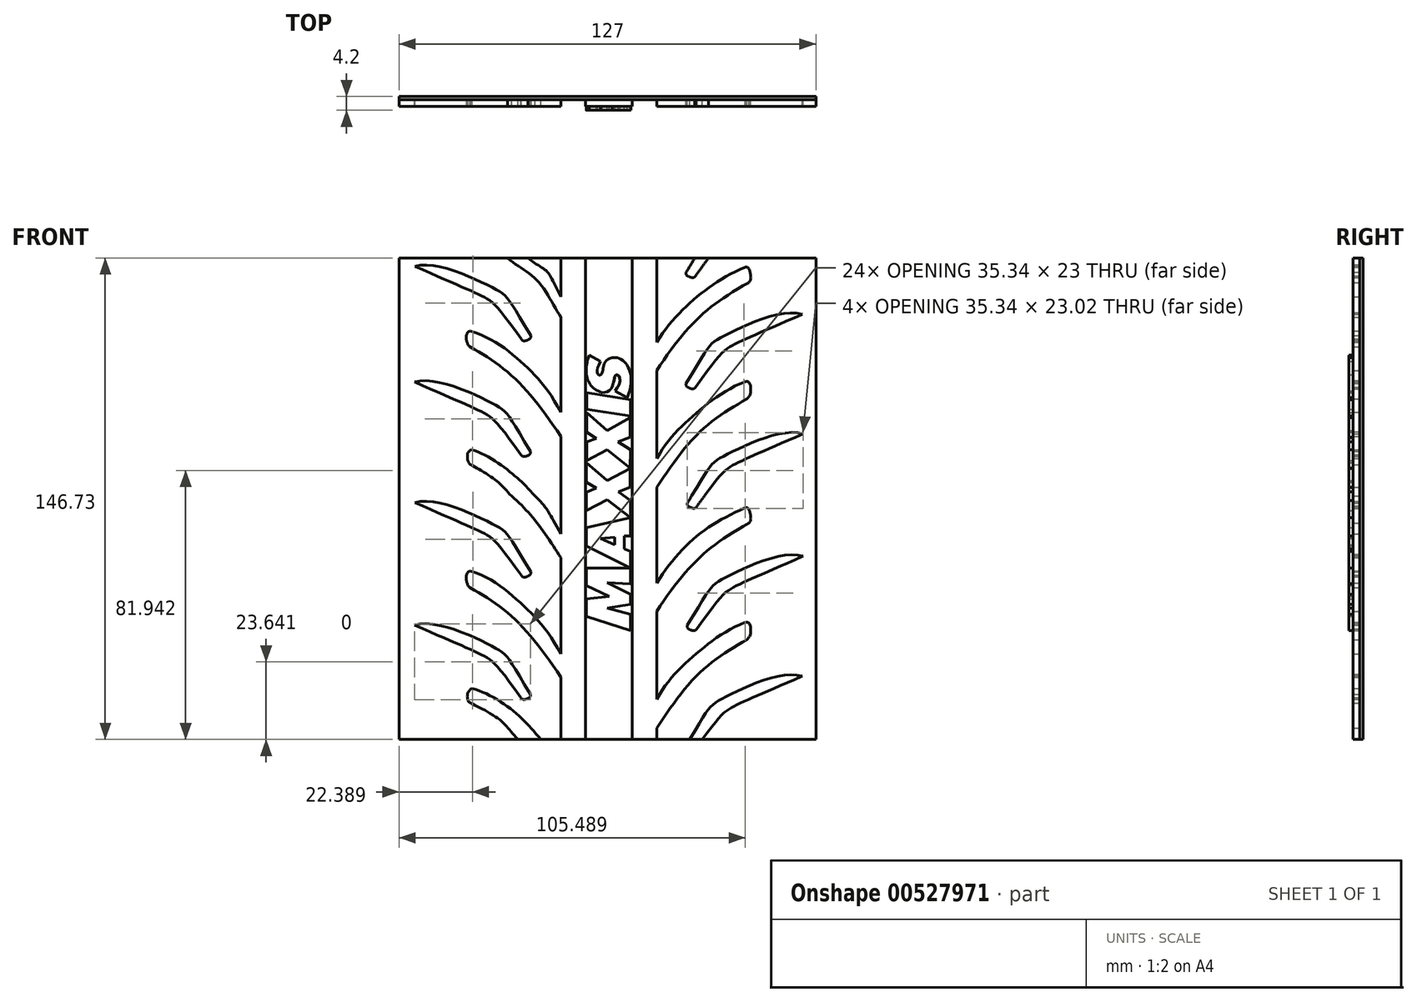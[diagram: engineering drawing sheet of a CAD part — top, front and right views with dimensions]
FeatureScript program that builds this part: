
annotation { "Feature Type Name" : "Feature", "Feature Type Description" : "" }
export const myFeature = defineFeature(function(context is Context, id is Id, definition is map)
    precondition{}
    {
        {
            var Q0;
            Q0=qCreatedBy(makeId("Front.planeOp"),FACE);
            var sketch = newSketch(context, id + "F0", { "sketchPlane" : qUnion([Q0])});
            skFitSpline(sketch, "E0", {"points": [v(-41.87, 15.25) * mm, v(-26, 5.1) * mm, v(-14.16, -10.06) * mm], "startDerivative": vector(39.83, -11.03) * mm, "endDerivative": vector(22.53, -43.37) * mm});
            skFitSpline(sketch, "E1", {"points": [v(-41.87, 15.25) * mm, v(-41.87, 10.2) * mm], "startDerivative": vector(-5.4, -1.6) * mm, "endDerivative": vector(3.38, -2.64) * mm});
            skFitSpline(sketch, "E2", {"points": [v(-41.87, 10.2) * mm, v(-28.68, 1) * mm, v(-14.16, -17.08) * mm], "startDerivative": vector(31.36, -16.8) * mm, "endDerivative": vector(27.1, -40.96) * mm});
            skLineSegment(sketch, "E3", {"start": v(-14.16, 38.05) * mm, "end": v(-14.16, -36.07) * mm});
            skLineSegment(sketch, "E4", {"start": v(-63.45, 38.05) * mm, "end": v(-63.45, -36.07) * mm});
            skLineSegment(sketch, "E5", {"start": v(63.55, 38.05) * mm, "end": v(63.55, -36.07) * mm});
            skLineSegment(sketch, "E6", {"start": v(-6.66, 38.05) * mm, "end": v(-6.66, -36.07) * mm});
            skLineSegment(sketch, "E7", {"start": v(7.57, 38.05) * mm, "end": v(7.57, -36.07) * mm});
            skFitSpline(sketch, "E8", {"points": [v(-14.16, 19.32) * mm, v(-21.42, 29.93) * mm, v(-29.1, 38.05) * mm], "startDerivative": vector(-12.47, 19.94) * mm, "endDerivative": vector(-18.22, 16) * mm});
            skFitSpline(sketch, "E9", {"points": [v(-14.16, 26.5) * mm, v(-19.3, 35.18) * mm, v(-22, 38.05) * mm], "startDerivative": vector(-15.52, 29.56) * mm, "endDerivative": vector(-10.56, 9.36) * mm});
            skLineSegment(sketch, "E10", {"start": v(-63.45, 38.05) * mm, "end": v(-14.16, 38.05) * mm});
            skLineSegment(sketch, "E11", {"start": v(-6.66, 38.05) * mm, "end": v(7.57, 38.05) * mm});
            skLineSegment(sketch, "E12", {"start": v(-6.66, -36.07) * mm, "end": v(7.57, -36.07) * mm});
            skLineSegment(sketch, "E13", {"start": v(-63.45, -36.07) * mm, "end": v(-14.16, -36.07) * mm});
            skFitSpline(sketch, "E14", {"points": [v(-41.21, -20.51) * mm, v(-28.56, -27.44) * mm, v(-20.21, -36.07) * mm], "startDerivative": vector(23.59, -6.3) * mm, "endDerivative": vector(17.58, -20.04) * mm});
            skFitSpline(sketch, "E15", {"points": [v(-41.61, -24.98) * mm, v(-32.51, -30.3) * mm, v(-27.2, -36.07) * mm], "startDerivative": vector(12.42, -6.2) * mm, "endDerivative": vector(15.61, -15.43) * mm});
            skFitSpline(sketch, "E16", {"points": [v(-41.21, -20.51) * mm, v(-42.62, -23.46) * mm, v(-41.61, -24.98) * mm], "startDerivative": vector(-7.34, -4.9) * mm, "endDerivative": vector(5.07, -2.11) * mm});
            skLineSegment(sketch, "E17", {"start": v(7.57, 38.05) * mm, "end": v(63.55, 38.05) * mm});
            skLineSegment(sketch, "E18", {"start": v(7.57, -36.07) * mm, "end": v(63.55, -36.07) * mm});
            skLineSegment(sketch, "E19", {"start": v(15.07, 38.05) * mm, "end": v(15.07, -36.07) * mm});
            skFitSpline(sketch, "E20", {"points": [v(15.07, 11.59) * mm, v(26.82, 25.46) * mm, v(42, 34.51) * mm], "startDerivative": vector(20, 32.91) * mm, "endDerivative": vector(36.18, 15.5) * mm});
            skFitSpline(sketch, "E21", {"points": [v(15.07, 2.95) * mm, v(28.1, 19.3) * mm, v(43.15, 29.82) * mm], "startDerivative": vector(23.95, 38.61) * mm, "endDerivative": vector(42.2, 23.64) * mm});
            skFitSpline(sketch, "E22", {"points": [v(42, 34.51) * mm, v(43.56, 32.58) * mm, v(43.15, 29.82) * mm], "startDerivative": vector(7.11, 1.27) * mm, "endDerivative": vector(-4.32, -4.08) * mm});
            skFitSpline(sketch, "E23", {"points": [v(15.07, -23.83) * mm, v(26.27, -10.7) * mm, v(41.97, -0.42) * mm], "startDerivative": vector(18.66, 34.39) * mm, "endDerivative": vector(36.86, 14.29) * mm});
            skFitSpline(sketch, "E24", {"points": [v(15.07, -32.63) * mm, v(28.33, -15.58) * mm, v(42.51, -5.65) * mm], "startDerivative": vector(23.07, 34.96) * mm, "endDerivative": vector(31.15, 18.27) * mm});
            skFitSpline(sketch, "E25", {"points": [v(41.97, -0.42) * mm, v(43.69, -2.52) * mm, v(42.51, -5.65) * mm], "startDerivative": vector(9.3, 2.66) * mm, "endDerivative": vector(-6.7, -6.41) * mm});
            skFitSpline(sketch, "E26", {"points": [v(-41.87, 88.4) * mm, v(-26, 78.77) * mm, v(-14.16, 63.62) * mm], "startDerivative": vector(39.83, -11.03) * mm, "endDerivative": vector(22.53, -43.37) * mm});
            skFitSpline(sketch, "E27", {"points": [v(-41.87, 88.4) * mm, v(-41.87, 83.57) * mm], "startDerivative": vector(-5.4, -1.6) * mm, "endDerivative": vector(3.38, -2.64) * mm});
            skFitSpline(sketch, "E28", {"points": [v(-41.87, 83.57) * mm, v(-28.68, 74.37) * mm, v(-14.16, 56.3) * mm], "startDerivative": vector(31.36, -16.8) * mm, "endDerivative": vector(27.1, -40.96) * mm});
            skLineSegment(sketch, "E29", {"start": v(-14.16, 110.66) * mm, "end": v(-14.16, 38.05) * mm});
            skLineSegment(sketch, "E30", {"start": v(-63.45, 110.66) * mm, "end": v(-63.45, 38.05) * mm});
            skLineSegment(sketch, "E31", {"start": v(63.55, 110.66) * mm, "end": v(63.55, 38.05) * mm});
            skFitSpline(sketch, "E32", {"points": [v(-58.73, 72.86) * mm, v(-34.7, 66.14) * mm, v(-23.42, 51.76) * mm], "startDerivative": vector(36.72, 11.37) * mm, "endDerivative": vector(46.72, -77.02) * mm});
            skFitSpline(sketch, "E33", {"points": [v(-58.73, 72.86) * mm, v(-38.18, 63.75) * mm, v(-26.28, 50.69) * mm], "startDerivative": vector(58.42, -25.77) * mm, "endDerivative": vector(47.5, -66.35) * mm});
            skFitSpline(sketch, "E34", {"points": [v(-26.28, 50.69) * mm, v(-24.63, 50.28) * mm, v(-23.42, 51.76) * mm], "startDerivative": vector(2.58, -4.3) * mm, "endDerivative": vector(-1.55, 4.54) * mm});
            skLineSegment(sketch, "E35", {"start": v(-6.66, 110.66) * mm, "end": v(-6.66, 38.05) * mm});
            skLineSegment(sketch, "E36", {"start": v(7.57, 110.66) * mm, "end": v(7.57, 38.05) * mm});
            skFitSpline(sketch, "E37", {"points": [v(-14.16, 92.58) * mm, v(-21.5, 103.91) * mm, v(-30.42, 110.66) * mm], "startDerivative": vector(-12.47, 19.94) * mm, "endDerivative": vector(-18.22, 16) * mm});
            skFitSpline(sketch, "E38", {"points": [v(-14.16, 98.84) * mm, v(-18.85, 106.94) * mm, v(-24.2, 110.66) * mm], "startDerivative": vector(-15.52, 29.56) * mm, "endDerivative": vector(-10.56, 9.36) * mm});
            skLineSegment(sketch, "E39", {"start": v(-63.45, 110.66) * mm, "end": v(-14.16, 110.66) * mm});
            skLineSegment(sketch, "E40", {"start": v(-6.66, 110.66) * mm, "end": v(7.57, 110.66) * mm});
            skFitSpline(sketch, "E41", {"points": [v(-41.45, 52.27) * mm, v(-29.45, 45.33) * mm, v(-22, 38.05) * mm], "startDerivative": vector(23.59, -6.3) * mm, "endDerivative": vector(17.58, -20.04) * mm});
            skFitSpline(sketch, "E42", {"points": [v(-41.59, 47.7) * mm, v(-33.15, 42.24) * mm, v(-29.1, 38.05) * mm], "startDerivative": vector(12.42, -6.2) * mm, "endDerivative": vector(15.61, -15.43) * mm});
            skFitSpline(sketch, "E43", {"points": [v(-41.45, 52.27) * mm, v(-42.62, 49.91) * mm, v(-41.59, 47.7) * mm], "startDerivative": vector(-7.34, -4.9) * mm, "endDerivative": vector(5.07, -2.11) * mm});
            skLineSegment(sketch, "E44", {"start": v(7.57, 110.66) * mm, "end": v(63.55, 110.66) * mm});
            skLineSegment(sketch, "E45", {"start": v(15.07, 110.66) * mm, "end": v(15.07, 38.05) * mm});
            skFitSpline(sketch, "E46", {"points": [v(15.07, 84.96) * mm, v(26.86, 98.46) * mm, v(42, 107.88) * mm], "startDerivative": vector(20, 32.91) * mm, "endDerivative": vector(36.18, 15.5) * mm});
            skFitSpline(sketch, "E47", {"points": [v(15.07, 76.32) * mm, v(28.1, 92.66) * mm, v(43.15, 103.2) * mm], "startDerivative": vector(23.95, 38.61) * mm, "endDerivative": vector(42.2, 23.64) * mm});
            skFitSpline(sketch, "E48", {"points": [v(42, 107.88) * mm, v(43.56, 105.95) * mm, v(43.15, 103.2) * mm], "startDerivative": vector(7.11, 1.27) * mm, "endDerivative": vector(-4.32, -4.08) * mm});
            skFitSpline(sketch, "E49", {"points": [v(15.07, 49.54) * mm, v(26.27, 62.68) * mm, v(41.97, 72.95) * mm], "startDerivative": vector(18.66, 34.39) * mm, "endDerivative": vector(36.86, 14.29) * mm});
            skFitSpline(sketch, "E50", {"points": [v(15.07, 40.74) * mm, v(28.33, 57.79) * mm, v(42.51, 67.72) * mm], "startDerivative": vector(23.07, 34.96) * mm, "endDerivative": vector(31.15, 18.27) * mm});
            skFitSpline(sketch, "E51", {"points": [v(41.97, 72.95) * mm, v(43.69, 70.85) * mm, v(42.51, 67.72) * mm], "startDerivative": vector(9.3, 2.66) * mm, "endDerivative": vector(-6.7, -6.41) * mm});
            skFitSpline(sketch, "E52", {"points": [v(-58.63, 108.12) * mm, v(-34.6, 101.41) * mm, v(-23.32, 87.02) * mm], "startDerivative": vector(36.72, 11.37) * mm, "endDerivative": vector(46.72, -77.02) * mm});
            skFitSpline(sketch, "E53", {"points": [v(-58.63, 108.12) * mm, v(-38.08, 99.01) * mm, v(-26.18, 85.95) * mm], "startDerivative": vector(58.42, -25.77) * mm, "endDerivative": vector(47.5, -66.35) * mm});
            skFitSpline(sketch, "E54", {"points": [v(-26.18, 85.95) * mm, v(-24.53, 85.55) * mm, v(-23.32, 87.02) * mm], "startDerivative": vector(2.58, -4.3) * mm, "endDerivative": vector(-1.55, 4.54) * mm});
            skFitSpline(sketch, "E55", {"points": [v(-58.63, 36.1) * mm, v(-34.6, 29.4) * mm, v(-23.32, 15) * mm], "startDerivative": vector(36.72, 11.37) * mm, "endDerivative": vector(46.72, -77.02) * mm});
            skFitSpline(sketch, "E56", {"points": [v(-58.63, 36.1) * mm, v(-38.08, 27) * mm, v(-26.18, 13.93) * mm], "startDerivative": vector(58.42, -25.77) * mm, "endDerivative": vector(47.5, -66.35) * mm});
            skFitSpline(sketch, "E57", {"points": [v(-26.18, 13.93) * mm, v(-24.53, 13.53) * mm, v(-23.32, 15) * mm], "startDerivative": vector(2.58, -4.3) * mm, "endDerivative": vector(-1.55, 4.54) * mm});
            skFitSpline(sketch, "E58", {"points": [v(-58.73, -1.2) * mm, v(-34.7, -7.91) * mm, v(-23.42, -22.3) * mm], "startDerivative": vector(36.72, 11.37) * mm, "endDerivative": vector(46.72, -77.02) * mm});
            skFitSpline(sketch, "E59", {"points": [v(-58.73, -1.2) * mm, v(-38.18, -10.31) * mm, v(-26.28, -23.37) * mm], "startDerivative": vector(58.42, -25.77) * mm, "endDerivative": vector(47.5, -66.35) * mm});
            skFitSpline(sketch, "E60", {"points": [v(-26.28, -23.37) * mm, v(-24.63, -23.78) * mm, v(-23.42, -22.3) * mm], "startDerivative": vector(2.58, -4.3) * mm, "endDerivative": vector(-1.55, 4.54) * mm});
            skFitSpline(sketch, "E61.MirrorCS", {"points": [v(59.33, -16.8) * mm, v(35.3, -23.5) * mm, v(24.02, -37.9) * mm], "startDerivative": vector(-36.72, 11.37) * mm, "endDerivative": vector(-46.72, -77.02) * mm});
            skFitSpline(sketch, "E62.MirrorCS", {"points": [v(59.33, -16.8) * mm, v(38.78, -25.9) * mm, v(26.88, -38.97) * mm], "startDerivative": vector(-58.42, -25.77) * mm, "endDerivative": vector(-47.5, -66.35) * mm});
            skFitSpline(sketch, "E63.MirrorCS", {"points": [v(59.7, 19.78) * mm, v(35.67, 13.07) * mm, v(24.4, -1.31) * mm], "startDerivative": vector(-36.72, 11.37) * mm, "endDerivative": vector(-46.72, -77.02) * mm});
            skFitSpline(sketch, "E64.MirrorCS", {"points": [v(59.7, 19.78) * mm, v(39.15, 10.68) * mm, v(27.26, -2.39) * mm], "startDerivative": vector(-58.42, -25.77) * mm, "endDerivative": vector(-47.5, -66.35) * mm});
            skFitSpline(sketch, "E65.MirrorCS", {"points": [v(27.26, -2.39) * mm, v(25.6, -2.8) * mm, v(24.4, -1.31) * mm], "startDerivative": vector(-2.58, -4.3) * mm, "endDerivative": vector(1.55, 4.54) * mm});
            skFitSpline(sketch, "E66.MirrorCS", {"points": [v(59.7, 57.09) * mm, v(35.67, 50.38) * mm, v(24.4, 35.99) * mm], "startDerivative": vector(-36.72, 11.37) * mm, "endDerivative": vector(-46.72, -77.02) * mm});
            skFitSpline(sketch, "E67.MirrorCS", {"points": [v(59.7, 57.09) * mm, v(39.15, 47.98) * mm, v(27.26, 34.92) * mm], "startDerivative": vector(-58.42, -25.77) * mm, "endDerivative": vector(-47.5, -66.35) * mm});
            skFitSpline(sketch, "E68.MirrorCS", {"points": [v(27.26, 34.92) * mm, v(25.6, 34.51) * mm, v(24.4, 35.99) * mm], "startDerivative": vector(-2.58, -4.3) * mm, "endDerivative": vector(1.55, 4.54) * mm});
            skFitSpline(sketch, "E69.MirrorCS", {"points": [v(59.33, 93.5) * mm, v(35.3, 86.78) * mm, v(24.02, 72.4) * mm], "startDerivative": vector(-36.72, 11.37) * mm, "endDerivative": vector(-46.72, -77.02) * mm});
            skFitSpline(sketch, "E70.MirrorCS", {"points": [v(59.33, 93.5) * mm, v(38.78, 84.38) * mm, v(26.88, 71.32) * mm], "startDerivative": vector(-58.42, -25.77) * mm, "endDerivative": vector(-47.5, -66.35) * mm});
            skFitSpline(sketch, "E71.MirrorCS", {"points": [v(26.88, 71.32) * mm, v(25.23, 70.91) * mm, v(24.02, 72.4) * mm], "startDerivative": vector(-2.58, -4.3) * mm, "endDerivative": vector(1.55, 4.54) * mm});
            skFitSpline(sketch, "E72.MirrorCS", {"points": [v(59.33, 127.38) * mm, v(35.3, 120.67) * mm, v(24.02, 106.28) * mm], "startDerivative": vector(-36.72, 11.37) * mm, "endDerivative": vector(-46.72, -77.02) * mm});
            skFitSpline(sketch, "E73.MirrorCS", {"points": [v(59.33, 127.38) * mm, v(38.78, 118.27) * mm, v(26.88, 105.2) * mm], "startDerivative": vector(-58.42, -25.77) * mm, "endDerivative": vector(-47.5, -66.35) * mm});
            skFitSpline(sketch, "E74.MirrorCS", {"points": [v(26.88, 105.2) * mm, v(25.23, 104.8) * mm, v(24.02, 106.28) * mm], "startDerivative": vector(-2.58, -4.3) * mm, "endDerivative": vector(1.55, 4.54) * mm});
            skSolve(sketch);
        }
        {
            var Q0;
            {var subQ5=sQuery(id+"F0.wireOp",EDGE,"E0");Q0=makeQuery(id+"F0.imprint","IMPRINT",FACE,{"disambiguationData":[TD([[makeQuery(id+"F0.imprint","IMPRINT",EDGE,{"derivedFrom":subQ5}),1.0]])]});}
            var Q1;
            {var subQ3=sQuery(id+"F0.wireOp",EDGE,"E9");Q1=makeQuery(id+"F0.imprint","IMPRINT",FACE,{"disambiguationData":[TD([[makeQuery(id+"F0.imprint","IMPRINT",EDGE,{"derivedFrom":subQ3}),-1.0]])]});}
            var Q2;
            Q2=makeQuery(id+"F0.imprint","IMPRINT",FACE,{"disambiguationData":[TD([[makeQuery(id+"F0.imprint","IMPRINT",EDGE,{"derivedFrom":sQuery(id+"F0.wireOp",EDGE,"E6")}),1.0]])]});
            var Q3;
            {var subQ10=sQuery(id+"F0.wireOp",EDGE,"E5");Q3=makeQuery(id+"F0.imprint","IMPRINT",FACE,{"disambiguationData":[TD([[makeQuery(id+"F0.imprint","IMPRINT",EDGE,{"derivedFrom":subQ10}),-1.0]])]});}
            var Q4;
            {var subQ8=sQuery(id+"F0.wireOp",EDGE,"E31");Q4=makeQuery(id+"F0.imprint","IMPRINT",FACE,{"disambiguationData":[TD([[makeQuery(id+"F0.imprint","IMPRINT",EDGE,{"derivedFrom":subQ8}),-1.0]])]});}
            var Q5;
            Q5=makeQuery(id+"F0.imprint","IMPRINT",FACE,{"disambiguationData":[TD([[makeQuery(id+"F0.imprint","IMPRINT",EDGE,{"derivedFrom":sQuery(id+"F0.wireOp",EDGE,"E35")}),1.0]])]});
            var Q6;
            {var subQ3=sQuery(id+"F0.wireOp",EDGE,"E38");Q6=makeQuery(id+"F0.imprint","IMPRINT",FACE,{"disambiguationData":[TD([[makeQuery(id+"F0.imprint","IMPRINT",EDGE,{"derivedFrom":subQ3}),-1.0]])]});}
            var Q7;
            {var subQ5=sQuery(id+"F0.wireOp",EDGE,"E26");Q7=makeQuery(id+"F0.imprint","IMPRINT",FACE,{"disambiguationData":[TD([[makeQuery(id+"F0.imprint","IMPRINT",EDGE,{"derivedFrom":subQ5}),1.0]])]});}
            extrude(context, id + "F1", {"entities" : qUnion([Q0, Q1, Q2, Q3, Q4, Q5, Q6, Q7]), "depth" : 2 * mm, "offsetDistance" : 25 * mm});
        }
        {
            var Q0;
            Q0=makeQuery(id+"F1.opExtrude","CAP_FACE",FACE,{"disambiguationData":[OSD([sQuery(id+"F0.wireOp",EDGE,"E6"),sQuery(id+"F0.wireOp",EDGE,"E7"),sQuery(id+"F0.wireOp",EDGE,"E12"),sQuery(id+"F0.wireOp",EDGE,"E35"),sQuery(id+"F0.wireOp",EDGE,"E36"),sQuery(id+"F0.wireOp",EDGE,"E40")])],"isStart":false});
            var sketch = newSketch(context, id + "F2", { "sketchPlane" : qUnion([Q0])});
            skLineSegment(sketch, "E75", {"start": v(7.05, -2.85) * mm, "end": v(-6.34, 1.38) * mm});
            skLineSegment(sketch, "E76", {"start": v(-6.34, 1.38) * mm, "end": v(-6.34, 6.79) * mm});
            skLineSegment(sketch, "E77", {"start": v(-6.34, 6.79) * mm, "end": v(0.58, 7.57) * mm});
            skLineSegment(sketch, "E78", {"start": v(0.58, 7.57) * mm, "end": v(-6.34, 10.78) * mm});
            skLineSegment(sketch, "E79", {"start": v(-6.34, 10.78) * mm, "end": v(-6.34, 16.09) * mm});
            skLineSegment(sketch, "E80", {"start": v(-6.34, 16.09) * mm, "end": v(7.05, 16.09) * mm});
            skLineSegment(sketch, "E81", {"start": v(7.05, 16.13) * mm, "end": v(-6.34, 22.83) * mm});
            skLineSegment(sketch, "E82", {"start": v(-6.34, 22.83) * mm, "end": v(-6.34, 28.5) * mm});
            skLineSegment(sketch, "E83", {"start": v(-6.34, 28.5) * mm, "end": v(7.05, 31.45) * mm});
            skLineSegment(sketch, "E84", {"start": v(7.05, 31.46) * mm, "end": v(0, 36.94) * mm});
            skLineSegment(sketch, "E85", {"start": v(0, 36.94) * mm, "end": v(-6.34, 33.64) * mm});
            skLineSegment(sketch, "E86", {"start": v(-6.34, 33.64) * mm, "end": v(-6.34, 39.3) * mm});
            skLineSegment(sketch, "E87", {"start": v(-6.34, 39.3) * mm, "end": v(-3.34, 40.48) * mm});
            skLineSegment(sketch, "E88", {"start": v(-2.06, 25.1) * mm, "end": v(2.24, 25.5) * mm});
            skLineSegment(sketch, "E89", {"start": v(2.24, 25.5) * mm, "end": v(2.24, 23.32) * mm});
            skLineSegment(sketch, "E90", {"start": v(2.24, 23.32) * mm, "end": v(-2.06, 25.1) * mm});
            skLineSegment(sketch, "E91", {"start": v(7.05, 31.45) * mm, "end": v(7.05, 25.95) * mm});
            skLineSegment(sketch, "E92", {"start": v(7.06, 25.95) * mm, "end": v(7.05, 25.95) * mm});
            skLineSegment(sketch, "E93", {"start": v(7.05, 16.1) * mm, "end": v(7.05, 11.37) * mm});
            skLineSegment(sketch, "E94", {"start": v(7.05, 11.37) * mm, "end": v(0, 11.64) * mm});
            skLineSegment(sketch, "E95", {"start": v(0, 11.64) * mm, "end": v(7.05, 8.09) * mm});
            skLineSegment(sketch, "E96", {"start": v(7.05, 8.09) * mm, "end": v(7.05, 5.04) * mm});
            skLineSegment(sketch, "E97", {"start": v(7.05, 5.04) * mm, "end": v(0, 3.98) * mm});
            skLineSegment(sketch, "E98", {"start": v(0, 3.98) * mm, "end": v(7.05, 2.04) * mm});
            skLineSegment(sketch, "E99", {"start": v(7.05, 2.04) * mm, "end": v(7.05, -2.85) * mm});
            skLineSegment(sketch, "E100", {"start": v(-3.34, 40.48) * mm, "end": v(-6.35, 42.27) * mm});
            skLineSegment(sketch, "E101", {"start": v(-6.35, 42.27) * mm, "end": v(-6.35, 48.34) * mm});
            skLineSegment(sketch, "E102", {"start": v(-6.35, 48.34) * mm, "end": v(0, 42.82) * mm});
            skLineSegment(sketch, "E103", {"start": v(0, 42.82) * mm, "end": v(6.97, 46.55) * mm});
            skLineSegment(sketch, "E104", {"start": v(6.97, 46.55) * mm, "end": v(6.97, 40.78) * mm});
            skLineSegment(sketch, "E105", {"start": v(6.97, 40.78) * mm, "end": v(3.44, 39.43) * mm});
            skLineSegment(sketch, "E106", {"start": v(3.44, 39.43) * mm, "end": v(7.05, 36.74) * mm});
            skLineSegment(sketch, "E107", {"start": v(7.05, 36.74) * mm, "end": v(7.05, 31.46) * mm});
            skLineSegment(sketch, "E108", {"start": v(7.05, 16.13) * mm, "end": v(7.05, 21.29) * mm});
            skLineSegment(sketch, "E109", {"start": v(7.05, 21.29) * mm, "end": v(5.18, 21.98) * mm});
            skLineSegment(sketch, "E110", {"start": v(5.18, 21.98) * mm, "end": v(5.18, 25.95) * mm});
            skLineSegment(sketch, "E111", {"start": v(5.18, 25.95) * mm, "end": v(7.05, 25.95) * mm});
            skLineSegment(sketch, "E112", {"start": v(-6.32, 48.92) * mm, "end": v(0, 52.23) * mm});
            skLineSegment(sketch, "E113", {"start": v(0, 52.23) * mm, "end": v(6.97, 46.56) * mm});
            skLineSegment(sketch, "E114", {"start": v(7, 52.23) * mm, "end": v(3.3, 54.64) * mm});
            skLineSegment(sketch, "E115", {"start": v(3.3, 54.64) * mm, "end": v(6.97, 56.08) * mm});
            skLineSegment(sketch, "E116", {"start": v(6.97, 56.08) * mm, "end": v(6.97, 61.96) * mm});
            skLineSegment(sketch, "E117", {"start": v(6.97, 61.96) * mm, "end": v(0, 58.07) * mm});
            skLineSegment(sketch, "E118", {"start": v(0, 58.07) * mm, "end": v(-6.27, 63.51) * mm});
            skLineSegment(sketch, "E119", {"start": v(-6.27, 63.51) * mm, "end": v(-6.27, 57.6) * mm});
            skLineSegment(sketch, "E120", {"start": v(-6.27, 57.6) * mm, "end": v(-3.28, 55.65) * mm});
            skLineSegment(sketch, "E121", {"start": v(-3.28, 55.65) * mm, "end": v(-6.27, 54.64) * mm});
            skLineSegment(sketch, "E122", {"start": v(-6.27, 54.64) * mm, "end": v(-6.32, 48.92) * mm});
            skLineSegment(sketch, "E123", {"start": v(6.97, 46.56) * mm, "end": v(7, 52.23) * mm});
            skLineSegment(sketch, "E124", {"start": v(7, 62.46) * mm, "end": v(-6.27, 64.51) * mm});
            skLineSegment(sketch, "E125", {"start": v(-6.27, 64.51) * mm, "end": v(-6.27, 69.64) * mm});
            skLineSegment(sketch, "E126", {"start": v(-6.27, 69.64) * mm, "end": v(7, 67.5) * mm});
            skLineSegment(sketch, "E127", {"start": v(7, 67.5) * mm, "end": v(7, 62.46) * mm});
            skLineSegment(sketch, "E128", {"start": v(2.35, 70.17) * mm, "end": v(6.08, 68.1) * mm});
            skLineSegment(sketch, "E129", {"start": v(-5.52, 81.07) * mm, "end": v(-2.07, 79.1) * mm});
            skFitSpline(sketch, "E130", {"points": [v(-5.52, 81.07) * mm, v(-5.9, 73.45) * mm, v(-1.6, 69.66) * mm], "startDerivative": vector(-6.26, -17.18) * mm, "endDerivative": vector(14.54, -4.06) * mm});
            skFitSpline(sketch, "E131", {"points": [v(-1.6, 69.66) * mm, v(2.55, 74.9) * mm, v(2.35, 70.17) * mm], "startDerivative": vector(22.18, -1.04) * mm, "endDerivative": vector(-18.47, -21.97) * mm});
            skFitSpline(sketch, "E132", {"points": [v(-2.07, 79.1) * mm, v(-1.76, 75.21) * mm, v(1.54, 80.32) * mm], "startDerivative": vector(-14.95, -26.05) * mm, "endDerivative": vector(19.35, 4.71) * mm});
            skFitSpline(sketch, "E133", {"points": [v(1.54, 80.32) * mm, v(6.86, 76.1) * mm, v(6.08, 68.1) * mm], "startDerivative": vector(17.7, 1.71) * mm, "endDerivative": vector(-6.26, -15.1) * mm});
            skSolve(sketch);
        }
        {
            var Q0;
            Q0=makeQuery(id+"F2.imprint","IMPRINT",FACE,{"disambiguationData":[TD([[makeQuery(id+"F2.imprint","IMPRINT",EDGE,{"derivedFrom":sQuery(id+"F2.wireOp",EDGE,"E128")}),1.0]])]});
            var Q1;
            Q1=makeQuery(id+"F2.imprint","IMPRINT",FACE,{"disambiguationData":[TD([[makeQuery(id+"F2.imprint","IMPRINT",EDGE,{"derivedFrom":sQuery(id+"F2.wireOp",EDGE,"E124")}),-1.0]])]});
            var Q2;
            Q2=makeQuery(id+"F2.imprint","IMPRINT",FACE,{"disambiguationData":[TD([[makeQuery(id+"F2.imprint","IMPRINT",EDGE,{"derivedFrom":sQuery(id+"F2.wireOp",EDGE,"E112")}),1.0]])]});
            var Q3;
            Q3=makeQuery(id+"F2.imprint","IMPRINT",FACE,{"disambiguationData":[TD([[makeQuery(id+"F2.imprint","IMPRINT",EDGE,{"derivedFrom":sQuery(id+"F2.wireOp",EDGE,"E81")}),-1.0]])]});
            var Q4;
            Q4=makeQuery(id+"F2.imprint","IMPRINT",FACE,{"disambiguationData":[TD([[makeQuery(id+"F2.imprint","IMPRINT",EDGE,{"derivedFrom":sQuery(id+"F2.wireOp",EDGE,"E75")}),-1.0]])]});
            var Q5;
            Q5=makeQuery(id+"F2.imprint","IMPRINT",FACE,{"disambiguationData":[TD([[makeQuery(id+"F2.imprint","IMPRINT",EDGE,{"derivedFrom":sQuery(id+"F2.wireOp",EDGE,"E84")}),-1.0]])]});
            extrude(context, id + "F3", {"entities" : qUnion([Q0, Q1, Q2, Q3, Q4, Q5]), "operationType" : NewBodyOperationType.ADD, "depth" : 1.2 * mm, "offsetDistance" : 25 * mm});
        }
        {
            var Q0;
            Q0=qCreatedBy(makeId("Front.planeOp"),FACE);
            var sketch = newSketch(context, id + "F4", { "sketchPlane" : qUnion([Q0])});
            skLineSegment(sketch, "E134.0", {"start": v(63.55, 110.66) * mm, "end": v(63.55, -36.07) * mm});
            skLineSegment(sketch, "E135.0", {"start": v(-63.45, 110.66) * mm, "end": v(-63.45, -36.07) * mm});
            skLineSegment(sketch, "E136", {"start": v(63.55, 110.66) * mm, "end": v(-63.45, 110.66) * mm});
            skLineSegment(sketch, "E137", {"start": v(63.55, -36.07) * mm, "end": v(-63.45, -36.07) * mm});
            skSolve(sketch);
        }
        {
            var Q0;
            Q0 = qSketchRegion(id + "F4", true);
            extrude(context, id + "F5", {"entities" : qUnion([Q0]), "oppositeDirection" : true, "depth" : 1 * mm, "offsetDistance" : 25 * mm});
        }
    });
